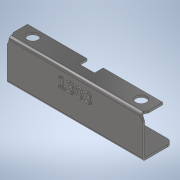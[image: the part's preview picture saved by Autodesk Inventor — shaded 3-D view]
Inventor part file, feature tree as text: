
AUTODESK INVENTOR PART (.ipt)
format: ipt  version: 2020 (Build 240168000, 168)  size: 575,488 bytes
history: native  units: mm
features: other x4, extrude x3, fillet x1, sketch x1, projected_geometry x1
ambient origin geometry x8: Origin, YZ Plane, XZ Plane, XY Plane, X Axis, Y Axis, Z Axis, Center Point
bodies: Body1 (feature_tree)
feature tree (10):
  other  "實體1"
  extrude  "擠出1"  Depth=124.7mm
  extrude  "擠出3"  Depth=26.3mm
  extrude  "擠出4"  Depth=33.0mm
  other  "折彎零件1"
  other  "折彎零件2"
  fillet  "圓角1"  Radius=17.0mm
  sketch  "草圖4"
  projected_geometry  "投影迴路1"
  other  "定義1"
